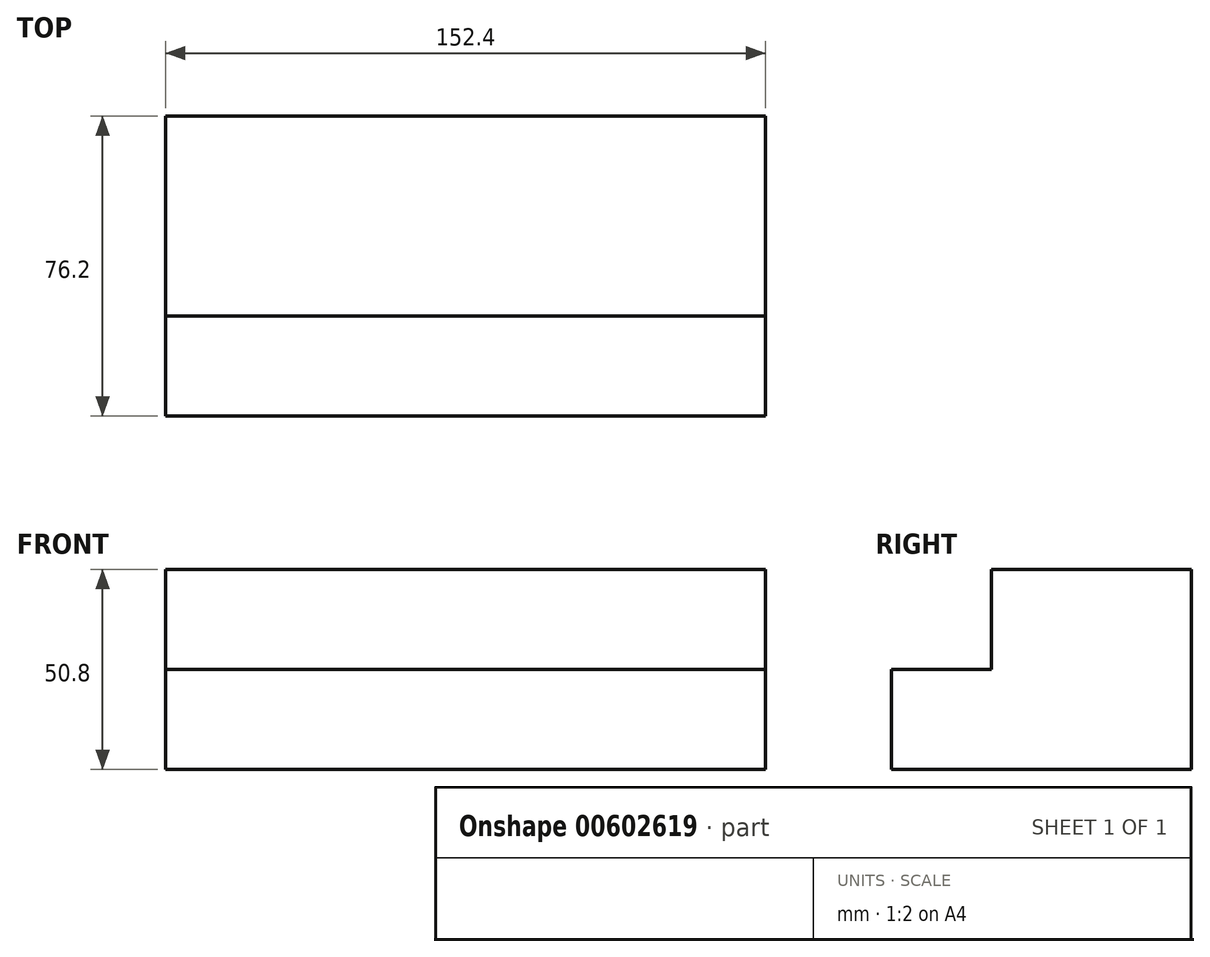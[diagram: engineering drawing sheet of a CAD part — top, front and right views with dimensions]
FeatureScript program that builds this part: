
annotation { "Feature Type Name" : "Feature", "Feature Type Description" : "" }
export const myFeature = defineFeature(function(context is Context, id is Id, definition is map)
    precondition{}
    {
        {
            var Q0;
            Q0=qCreatedBy(makeId("Right.planeOp"),FACE);
            var sketch = newSketch(context, id + "F0", { "sketchPlane" : qUnion([Q0])});
            skLineSegment(sketch, "E0", {"start": v(0, 0) * mm, "end": v(76.2, 0) * mm});
            skLineSegment(sketch, "E1", {"start": v(76.2, 0) * mm, "end": v(76.2, 50.8) * mm});
            skLineSegment(sketch, "E2", {"start": v(76.2, 50.8) * mm, "end": v(25.4, 50.8) * mm});
            skLineSegment(sketch, "E3", {"start": v(25.4, 50.8) * mm, "end": v(25.4, 25.4) * mm});
            skLineSegment(sketch, "E4", {"start": v(25.4, 25.4) * mm, "end": v(0, 25.4) * mm});
            skLineSegment(sketch, "E5", {"start": v(0, 25.4) * mm, "end": v(0, 0) * mm});
            skSolve(sketch);
        }
        {
            var Q0;
            Q0 = qSketchRegion(id + "F0", true);
            extrude(context, id + "F1", {"entities" : qUnion([Q0]), "depth" : 152.4 * mm, "offsetDistance" : 25.4 * mm});
        }
    });
